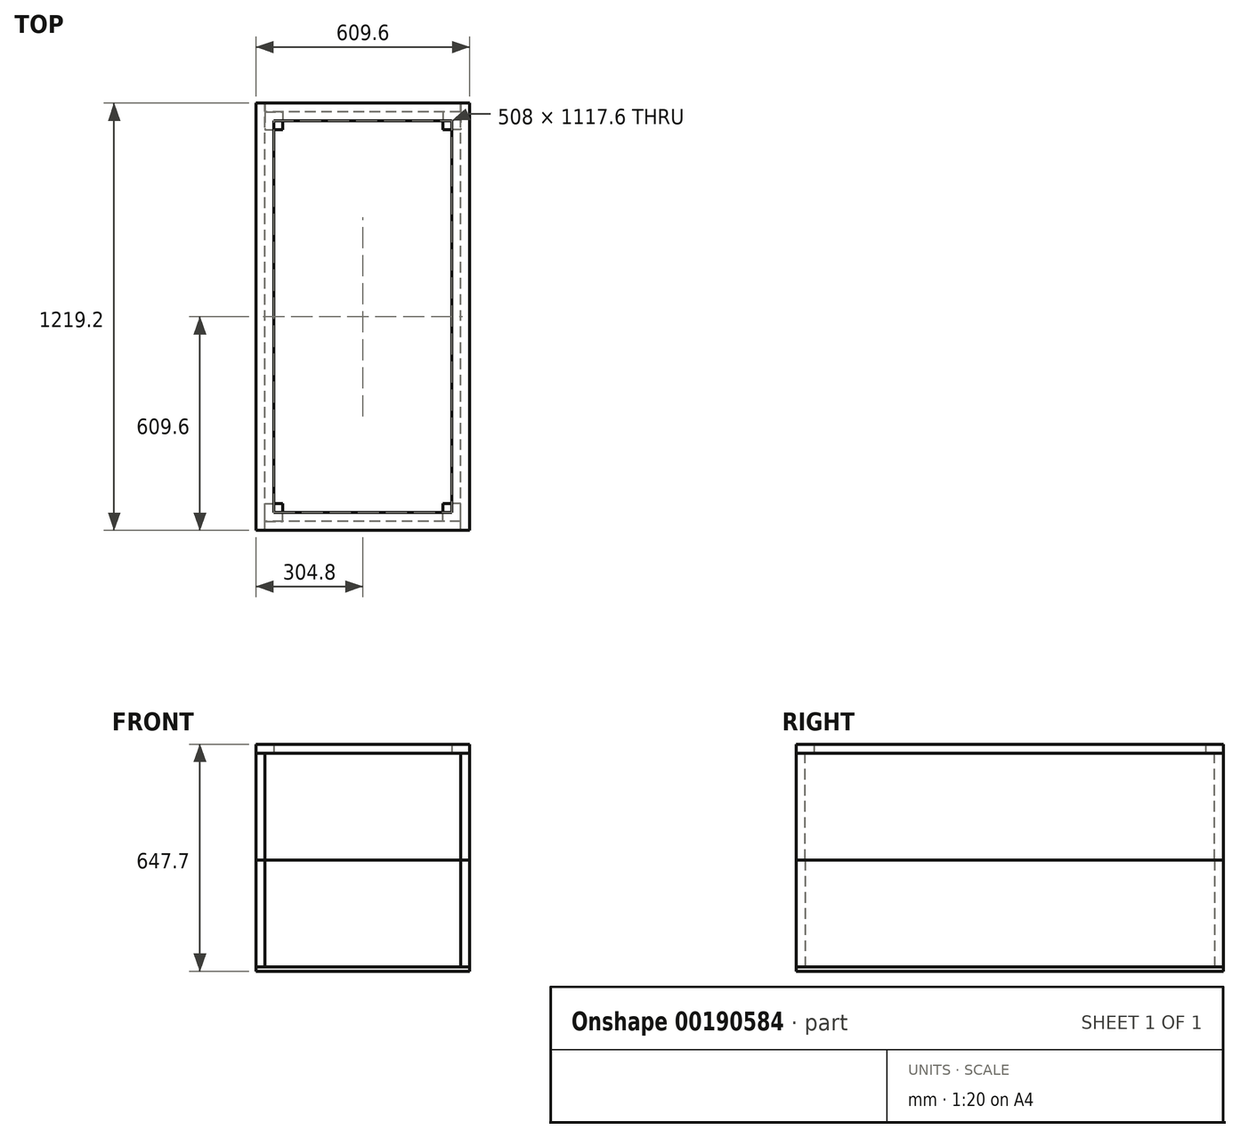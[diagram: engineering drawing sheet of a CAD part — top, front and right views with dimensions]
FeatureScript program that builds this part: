
annotation { "Feature Type Name" : "Feature", "Feature Type Description" : "" }
export const myFeature = defineFeature(function(context is Context, id is Id, definition is map)
    precondition{}
    {
        {
            var Q0;
            Q0=qCreatedBy(makeId("Top.planeOp"),FACE);
            var sketch = newSketch(context, id + "F0", { "sketchPlane" : qUnion([Q0])});
            skLineSegment(sketch, "E0.bottom", {"start": v(279.4, -584.2) * mm, "end": v(228.6, -584.2) * mm});
            skLineSegment(sketch, "E0.top", {"start": v(279.4, -533.4) * mm, "end": v(228.6, -533.4) * mm});
            skLineSegment(sketch, "E0.left", {"start": v(279.4, -584.2) * mm, "end": v(279.4, -533.4) * mm});
            skLineSegment(sketch, "E0.right", {"start": v(228.6, -584.2) * mm, "end": v(228.6, -533.4) * mm});
            skPoint(sketch, "E0.middle", {"position": v(254, -558.8) * mm});
            skLineSegment(sketch, "E1", {"start": v(0, 560.02) * mm, "end": v(0, -551.27) * mm, "construction": true});
            skLineSegment(sketch, "E2", {"start": v(-571.68, 0) * mm, "end": v(551.27, 0) * mm, "construction": true});
            skLineSegment(sketch, "E3.MirrorCS", {"start": v(-279.4, -584.2) * mm, "end": v(-228.6, -584.2) * mm});
            skPoint(sketch, "E4.MirrorP", {"position": v(-254, -558.8) * mm});
            skLineSegment(sketch, "E5.MirrorCS", {"start": v(-279.4, -533.4) * mm, "end": v(-228.6, -533.4) * mm});
            skLineSegment(sketch, "E6.MirrorCS", {"start": v(-228.6, -584.2) * mm, "end": v(-228.6, -533.4) * mm});
            skLineSegment(sketch, "E7.MirrorCS", {"start": v(-279.4, -584.2) * mm, "end": v(-279.4, -533.4) * mm});
            skLineSegment(sketch, "E8.MirrorCS", {"start": v(-228.6, 584.2) * mm, "end": v(-228.6, 533.4) * mm});
            skPoint(sketch, "E9.MirrorP", {"position": v(-254, 558.8) * mm});
            skLineSegment(sketch, "E10.MirrorCS", {"start": v(-279.4, 584.2) * mm, "end": v(-228.6, 584.2) * mm});
            skLineSegment(sketch, "E11.MirrorCS", {"start": v(279.4, 584.2) * mm, "end": v(279.4, 533.4) * mm});
            skLineSegment(sketch, "E12.MirrorCS", {"start": v(-279.4, 584.2) * mm, "end": v(-279.4, 533.4) * mm});
            skLineSegment(sketch, "E13.MirrorCS", {"start": v(-279.4, 533.4) * mm, "end": v(-228.6, 533.4) * mm});
            skPoint(sketch, "E14.MirrorP", {"position": v(254, 558.8) * mm});
            skLineSegment(sketch, "E15.MirrorCS", {"start": v(279.4, 584.2) * mm, "end": v(228.6, 584.2) * mm});
            skLineSegment(sketch, "E16.MirrorCS", {"start": v(279.4, 533.4) * mm, "end": v(228.6, 533.4) * mm});
            skLineSegment(sketch, "E17.MirrorCS", {"start": v(228.6, 584.2) * mm, "end": v(228.6, 533.4) * mm});
            skSolve(sketch);
        }
        {
            var Q0;
            Q0 = qSketchRegion(id + "F0", true);
            extrude(context, id + "F1", {"entities" : qUnion([Q0]), "depth" : 609.6 * mm});
        }
        {
            var Q0;
            Q0=makeQuery(id+"F1.opExtrude","SWEPT_FACE",FACE,{"disambiguationData":[OSD([sQuery(id+"F0.wireOp",EDGE,"E0.bottom")])]});
            var sketch = newSketch(context, id + "F2", { "sketchPlane" : qUnion([Q0])});
            skLineSegment(sketch, "E18.bottom", {"start": v(279.4, 0) * mm, "end": v(-279.4, 0) * mm});
            skLineSegment(sketch, "E18.top", {"start": v(279.4, 304.8) * mm, "end": v(-279.4, 304.8) * mm});
            skLineSegment(sketch, "E18.left", {"start": v(279.4, 0) * mm, "end": v(279.4, 304.8) * mm});
            skLineSegment(sketch, "E18.right", {"start": v(-279.4, 0) * mm, "end": v(-279.4, 304.8) * mm});
            skSolve(sketch);
        }
        {
            var Q0;
            Q0 = qSketchRegion(id + "F2", true);
            extrude(context, id + "F3", {"entities" : qUnion([Q0]), "depth" : 25.4 * mm});
        }
        {
            var Q0;
            Q0=makeQuery(id+"F3.opExtrude","SWEPT_BODY",BODY,{"disambiguationData":[OSD([sQuery(id+"F2.wireOp",EDGE,"E18.bottom"),sQuery(id+"F2.wireOp",EDGE,"E18.top"),sQuery(id+"F2.wireOp",EDGE,"E18.left"),sQuery(id+"F2.wireOp",EDGE,"E18.right")])]});
            var Q1;
            Q1=makeQuery(id+"F3.opExtrude","SWEPT_FACE",FACE,{"disambiguationData":[OSD([sQuery(id+"F2.wireOp",EDGE,"E18.top")])]});
            mirror(context, id + "F4", {"entities" : qUnion([Q0]), "mirrorPlane" : qUnion([Q1])});
        }
        {
            var Q0;
            Q0=makeQuery(id+"F4.opPattern","COPY",BODY,{"derivedFrom":makeQuery(id+"F3.opExtrude","SWEPT_BODY",BODY,{"disambiguationData":[OSD([sQuery(id+"F2.wireOp",EDGE,"E18.bottom"),sQuery(id+"F2.wireOp",EDGE,"E18.top"),sQuery(id+"F2.wireOp",EDGE,"E18.left"),sQuery(id+"F2.wireOp",EDGE,"E18.right")])]}),"instanceName":"1"});
            var Q1;
            Q1=makeQuery(id+"F3.opExtrude","SWEPT_BODY",BODY,{"disambiguationData":[OSD([sQuery(id+"F2.wireOp",EDGE,"E18.bottom"),sQuery(id+"F2.wireOp",EDGE,"E18.top"),sQuery(id+"F2.wireOp",EDGE,"E18.left"),sQuery(id+"F2.wireOp",EDGE,"E18.right")])]});
            var Q2;
            Q2=qCreatedBy(makeId("Front.planeOp"),FACE);
            mirror(context, id + "F5", {"entities" : qUnion([Q0, Q1]), "mirrorPlane" : qUnion([Q2])});
        }
        {
            var Q0;
            Q0=makeQuery(id+"F1.opExtrude","SWEPT_FACE",FACE,{"disambiguationData":[OSD([sQuery(id+"F0.wireOp",EDGE,"E7.MirrorCS")])]});
            var sketch = newSketch(context, id + "F6", { "sketchPlane" : qUnion([Q0])});
            skLineSegment(sketch, "E19.bottom", {"start": v(609.6, 0) * mm, "end": v(-609.6, 0) * mm});
            skLineSegment(sketch, "E19.top", {"start": v(609.6, 304.8) * mm, "end": v(-609.6, 304.8) * mm});
            skLineSegment(sketch, "E19.left", {"start": v(609.6, 0) * mm, "end": v(609.6, 304.8) * mm});
            skLineSegment(sketch, "E19.right", {"start": v(-609.6, 0) * mm, "end": v(-609.6, 304.8) * mm});
            skSolve(sketch);
        }
        {
            var Q0;
            Q0 = qSketchRegion(id + "F6", true);
            extrude(context, id + "F7", {"entities" : qUnion([Q0]), "depth" : 25.4 * mm});
        }
        {
            var Q0;
            Q0=makeQuery(id+"F7.opExtrude","SWEPT_BODY",BODY,{"disambiguationData":[OSD([sQuery(id+"F6.wireOp",EDGE,"E19.bottom"),sQuery(id+"F6.wireOp",EDGE,"E19.top"),sQuery(id+"F6.wireOp",EDGE,"E19.left"),sQuery(id+"F6.wireOp",EDGE,"E19.right")])]});
            var Q1;
            Q1=makeQuery(id+"F7.opExtrude","SWEPT_FACE",FACE,{"disambiguationData":[OSD([sQuery(id+"F6.wireOp",EDGE,"E19.top")])]});
            mirror(context, id + "F8", {"entities" : qUnion([Q0]), "mirrorPlane" : qUnion([Q1])});
        }
        {
            var Q0;
            Q0=makeQuery(id+"F7.opExtrude","SWEPT_BODY",BODY,{"disambiguationData":[OSD([sQuery(id+"F6.wireOp",EDGE,"E19.bottom"),sQuery(id+"F6.wireOp",EDGE,"E19.top"),sQuery(id+"F6.wireOp",EDGE,"E19.left"),sQuery(id+"F6.wireOp",EDGE,"E19.right")])]});
            var Q1;
            Q1=makeQuery(id+"F8.opPattern","COPY",BODY,{"derivedFrom":makeQuery(id+"F7.opExtrude","SWEPT_BODY",BODY,{"disambiguationData":[OSD([sQuery(id+"F6.wireOp",EDGE,"E19.bottom"),sQuery(id+"F6.wireOp",EDGE,"E19.top"),sQuery(id+"F6.wireOp",EDGE,"E19.left"),sQuery(id+"F6.wireOp",EDGE,"E19.right")])]}),"instanceName":"1"});
            var Q2;
            Q2=qCreatedBy(makeId("Right.planeOp"),FACE);
            mirror(context, id + "F9", {"entities" : qUnion([Q0, Q1]), "mirrorPlane" : qUnion([Q2])});
        }
        {
            var Q0;
            Q0=makeQuery(id+"F1.opExtrude","CAP_FACE",FACE,{"disambiguationData":[OSD([sQuery(id+"F0.wireOp",EDGE,"E0.bottom"),sQuery(id+"F0.wireOp",EDGE,"E0.top"),sQuery(id+"F0.wireOp",EDGE,"E0.left"),sQuery(id+"F0.wireOp",EDGE,"E0.right")])],"isStart":true});
            var sketch = newSketch(context, id + "F10", { "sketchPlane" : qUnion([Q0])});
            skLineSegment(sketch, "E20.bottom", {"start": v(304.8, 609.6) * mm, "end": v(-304.8, 609.6) * mm});
            skLineSegment(sketch, "E20.top", {"start": v(304.8, -609.6) * mm, "end": v(-304.8, -609.6) * mm});
            skLineSegment(sketch, "E20.left", {"start": v(304.8, 609.6) * mm, "end": v(304.8, -609.6) * mm});
            skLineSegment(sketch, "E20.right", {"start": v(-304.8, 609.6) * mm, "end": v(-304.8, -609.6) * mm});
            skSolve(sketch);
        }
        {
            var Q0;
            Q0 = qSketchRegion(id + "F10", true);
            extrude(context, id + "F11", {"entities" : qUnion([Q0]), "depth" : 12.7 * mm});
        }
        {
            var Q0;
            Q0=makeQuery(id+"F4.opPattern","COPY",FACE,{"derivedFrom":makeQuery(id+"F3.opExtrude","CAP_FACE",FACE,{"disambiguationData":[OSD([sQuery(id+"F2.wireOp",EDGE,"E18.bottom"),sQuery(id+"F2.wireOp",EDGE,"E18.top"),sQuery(id+"F2.wireOp",EDGE,"E18.left"),sQuery(id+"F2.wireOp",EDGE,"E18.right")])],"isStart":false}),"instanceName":"1"});
            var sketch = newSketch(context, id + "F12", { "sketchPlane" : qUnion([Q0])});
            skLineSegment(sketch, "E21.bottom", {"start": v(-304.8, 609.6) * mm, "end": v(304.8, 609.6) * mm});
            skLineSegment(sketch, "E21.top", {"start": v(-304.8, 304.8) * mm, "end": v(304.8, 304.8) * mm});
            skLineSegment(sketch, "E21.left", {"start": v(-304.8, 609.6) * mm, "end": v(-304.8, 304.8) * mm});
            skLineSegment(sketch, "E21.right", {"start": v(304.8, 609.6) * mm, "end": v(304.8, 304.8) * mm});
            skSolve(sketch);
        }
        {
            var Q0;
            Q0=makeQuery(id+"F1.opExtrude","CAP_FACE",FACE,{"disambiguationData":[OSD([sQuery(id+"F0.wireOp",EDGE,"E3.MirrorCS"),sQuery(id+"F0.wireOp",EDGE,"E5.MirrorCS"),sQuery(id+"F0.wireOp",EDGE,"E6.MirrorCS"),sQuery(id+"F0.wireOp",EDGE,"E7.MirrorCS")])],"isStart":false});
            var sketch = newSketch(context, id + "F13", { "sketchPlane" : qUnion([Q0])});
            skLineSegment(sketch, "E22.bottom", {"start": v(-304.8, -609.6) * mm, "end": v(-254, -609.6) * mm});
            skLineSegment(sketch, "E22.top", {"start": v(-304.8, 609.6) * mm, "end": v(-254, 609.6) * mm});
            skLineSegment(sketch, "E22.left", {"start": v(-304.8, -609.6) * mm, "end": v(-304.8, 609.6) * mm});
            skLineSegment(sketch, "E22.right", {"start": v(-254, -609.6) * mm, "end": v(-254, 609.6) * mm});
            skLineSegment(sketch, "E23.bottom", {"start": v(304.8, 609.6) * mm, "end": v(254, 609.6) * mm});
            skLineSegment(sketch, "E23.top", {"start": v(304.8, -609.6) * mm, "end": v(254, -609.6) * mm});
            skLineSegment(sketch, "E23.left", {"start": v(304.8, 609.6) * mm, "end": v(304.8, -609.6) * mm});
            skLineSegment(sketch, "E23.right", {"start": v(254, 609.6) * mm, "end": v(254, -609.6) * mm});
            skLineSegment(sketch, "E24.bottom", {"start": v(-254, -609.6) * mm, "end": v(254, -609.6) * mm});
            skLineSegment(sketch, "E24.top", {"start": v(-254, -558.8) * mm, "end": v(254, -558.8) * mm});
            skLineSegment(sketch, "E24.left", {"start": v(-254, -609.6) * mm, "end": v(-254, -558.8) * mm});
            skLineSegment(sketch, "E24.right", {"start": v(254, -609.6) * mm, "end": v(254, -558.8) * mm});
            skLineSegment(sketch, "E25.bottom", {"start": v(-254, 558.8) * mm, "end": v(254, 558.8) * mm});
            skLineSegment(sketch, "E25.top", {"start": v(-254, 609.6) * mm, "end": v(254, 609.6) * mm});
            skLineSegment(sketch, "E25.left", {"start": v(-254, 558.8) * mm, "end": v(-254, 609.6) * mm});
            skLineSegment(sketch, "E25.right", {"start": v(254, 558.8) * mm, "end": v(254, 609.6) * mm});
            skSolve(sketch);
        }
        {
            var Q0;
            Q0 = qSketchRegion(id + "F13", true);
            extrude(context, id + "F14", {"entities" : qUnion([Q0]), "depth" : 25.4 * mm});
        }
    });
